# Revit family: HVAC_Solar-Heating_Cordivari_Stratos-4S
name_source: partatom
category: Mechanical Equipment
revit_build: Autodesk Revit 2015 (Build: 20140606_1530(x64)
units: mm (PartAtom-declared; Revit-internal decimal feet)

## types (2) — shared parameters
Assembly Code = D3010700
BIMobject category = Solar Heating
BIMobject category code = hvac-solar-heating
BIMobject main category = HVAC
BIMobject main category code = hvac
Connessioni ACS = 1/2” F
Description = Il sistema termico solare STRATOS® 4S ROTOSHIELD® è un innovatvo sistema solare compato ad alta efcienza con accumulo sanitario integrato.
È dotato di un sistema autoequilibrante antstagnazione brevetato. Il breveto Rotoshield® protegge il sistema massimizzandone le performance. E’ indicato per la produzione di acqua calda sanitaria in tute le zone
climatche grazie alla sua capacità di preservare il calore captato. Il sistema può essere, infat, installato in zone con temperatura fno a -20°C.
Design country = Italy
Diameter = 25 mm  [stored 0.082021 ft]
Edition number = 1
Flow = 0.0 L/s
Inclinazione Falda = 10° - 70°
Installation instructions = http://www.cordivari.it
Keynote = 13600
Length = 2160 mm  [stored 7.08661 ft]
Manufacturer = Cordivari
Manufacturer country = Italy
Manufacturer name = Cordivari
Masterformat 2014 Code = 22 33 30.23
Masterformat 2014 Description = Residential, Collector-to-Tank, Solar-Electric Domestic Water Heaters
Material main = Aluminium
Material secondary = Steel
Model = Stratos - 4S
Nominal width = 2160 mm  [stored 7.08661 ft]
OmniClass Code = 23-33 53 11
OmniClass Description = Solar Water Heating Packaged Units
P. Max Accumulo = 7.5 bar
P. Max Ingreso = 4.0 bar
Product Guid = 29935d71-3906-4814-a276-f70f55391db7
Product Material = Cordivari-Aluminum-Anodized Silver
Product SKU = solar-system-stratos-4s
Product data url = https://bimobject.com
Product family = Integrated solar systems
Product group = Compact solar thermal system
Product url = http://www.cordivari.it
QR code = http://bimobject.com
Surface Material = Cordivari-Solar Collector Tube
T. Max = 100 °C
T.Min = -566 °C
Technical description = http://www.cordivari.it
UNSPSC Code = 40101807
URL = www.cordivari.it
Uniclass 2.0 Code = SS-60-40-40-80
Uniclass 2.0 Description = Solar Heating Systems
Uniclass 2015 Code = Ss_60_40_37_81
Uniclass 2015 Name = Solar heating systems
Weight Net (Kg) = 0
zero-valued in all types: Nominal height

## per-type parameters (varying)
| type | Codice | Model 120 Visibility | Model 180 Visibility | Panel Width | Peso | Superficie Lorda | Width | Y | Z |
| Modello 120 | 3410316603203 | Yes | No | 822 mm | 120.00 kg | 1.78 m² | 752 mm | 67 mm | 127 mm |
| Modello 180 | 3410316603204 | No | Yes | 1052 mm  [stored 3.45144 ft] | 180.00 kg | 2.27 m² | 951 mm | 125 mm  [stored 0.410105 ft] | 226 mm |

note: [stored X ft] marks values corroborated as IEEE doubles in the binary element streams (Revit-internal decimal feet)

## geometry (parser evidence)
native form markers: Sweep x9
no freeform markers — native parametric forms only
